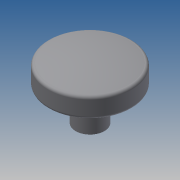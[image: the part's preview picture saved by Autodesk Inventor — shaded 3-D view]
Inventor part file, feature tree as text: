
AUTODESK INVENTOR PART (.ipt)
format: ipt  version: 2014 SP1 (Build 180222100, 222)  size: 270,848 bytes
history: native  units: in
note: dims shown in document units (in); Inventor stores cm internally (conversion verified against a paired STEP export)
features: sketch x6, extrude x5, plane x2, pattern_circular x1, revolve x1
ambient origin geometry x8: Origin, YZ Plane, XZ Plane, XY Plane, X Axis, Y Axis, Z Axis, Center Point
bodies: Solid1 (feature_tree)
feature tree (15):
  extrude  "Extrusion1"  Depth=0.05in
  sketch  "Sketch2"  dims[d2=8.0in d3=0.0in d4=0.5in]
  plane  "Work Plane1"
  extrude  "Extrusion2"  Depth=0.5in
  extrude  "Extrusion3"  Depth=0.5in
  pattern_circular  "Circular Pattern1"  Count=3 Angle=360.0deg
  plane  "Work Plane5"
  revolve  "Revolution3"  [1 undecoded]
  extrude  "Extrusion5"  Depth=4.0in
  extrude  "Extrusion6"  TaperAngle=90.0deg  [1 undecoded]
  sketch  "Sketch1"  dims[d0=6.0in d1=0.05in]
  sketch  "Sketch3"  dims[d5=0.75in d6=0.5in]
  sketch  "Sketch4"  dims[d7=0.05in d8=0.0in]
  sketch  "Sketch8"  dims[d9=0.05in]
  sketch  "Sketch11"  dims[d10=4.0in d11=0.0in d12=1.1811in d13=360.0deg d25=-0.25in d27=4.0in d30=90.0deg d34=6.5in d35=0.25in d36=0.0in d37=0.5in d38=0.0in d39=1.0in]
note: 2 required parameter values undecoded (feature->parameter linkage not recoverable at this tier; creation-order binding heuristic only, values carry confidence <= 0.55)